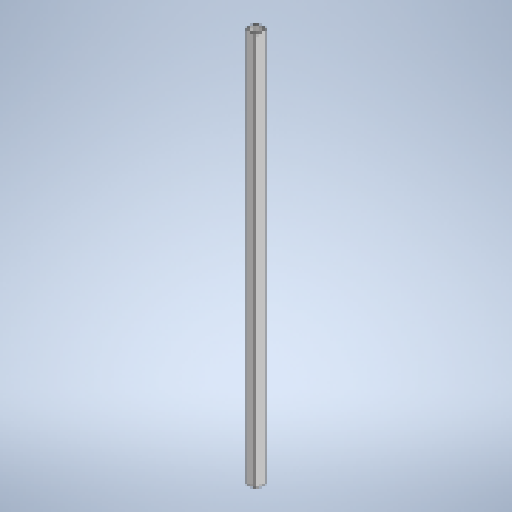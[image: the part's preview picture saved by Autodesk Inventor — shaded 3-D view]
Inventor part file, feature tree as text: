
AUTODESK INVENTOR PART (.ipt)
format: ipt  version: 2023 (Build 270158000, 158)  size: 141,312 bytes
history: native  units: in
note: dims shown in document units (in); Inventor stores cm internally (conversion verified against a paired STEP export)
features: extrude x1, sketch x1
ambient origin geometry x8: Origin, YZ Plane, XZ Plane, XY Plane, X Axis, Y Axis, Z Axis, Center Point
bodies: Solid1 (feature_tree)
feature tree (2):
  extrude  "Extrusion1"  Depth=0.0625in
  sketch  "Sketch1"  dims[d0=1.0in d1=0.0625in d2=0.0625in d3=0.0625in d4=37.7953in d5=0.0in]
